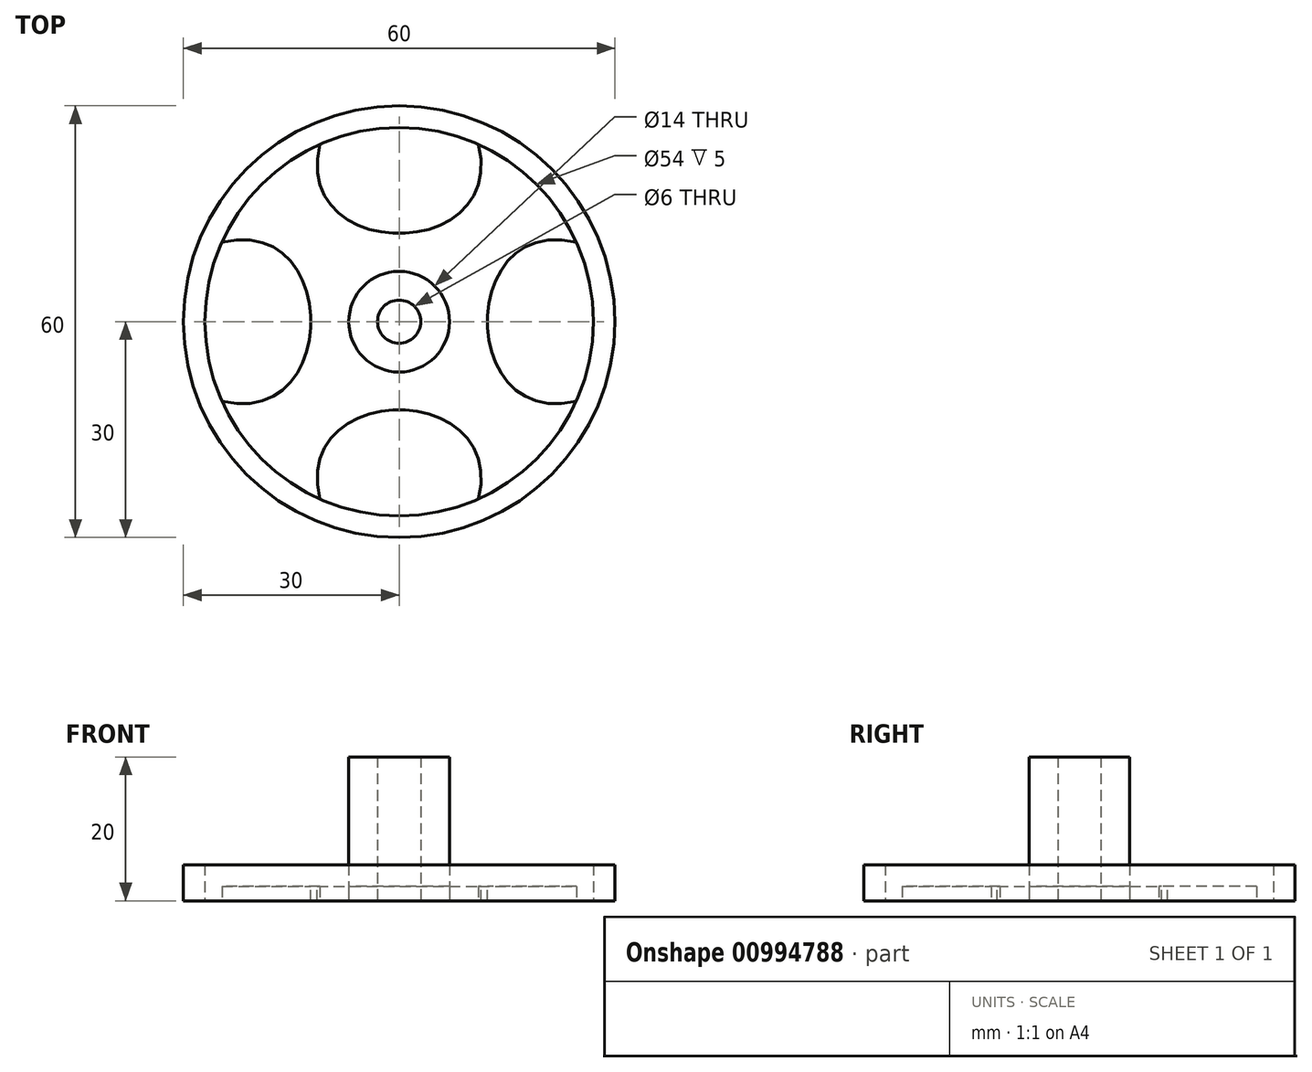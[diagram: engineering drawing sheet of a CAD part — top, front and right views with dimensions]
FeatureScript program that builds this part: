
annotation { "Feature Type Name" : "Feature", "Feature Type Description" : "" }
export const myFeature = defineFeature(function(context is Context, id is Id, definition is map)
    precondition{}
    {
        {
            var Q0;
            Q0=qCreatedBy(makeId("Top.planeOp"),FACE);
            var sketch = newSketch(context, id + "F0", { "sketchPlane" : qUnion([Q0])});
            skCircle(sketch, "E0", {"center": v(0, 0) * mm, "radius": 30 * mm});
            skCircle(sketch, "E1", {"center": v(0, 0) * mm, "radius": 27 * mm});
            skCircle(sketch, "E2", {"center": v(0, 0) * mm, "radius": 7 * mm});
            skCircle(sketch, "E3", {"center": v(0, 0) * mm, "radius": 3 * mm});
            skLineSegment(sketch, "E4", {"start": v(-43.77, 43.77) * mm, "end": v(46.4, -46.4) * mm, "construction": true});
            skLineSegment(sketch, "E5", {"start": v(40.6, 40.6) * mm, "end": v(-43.15, -43.15) * mm, "construction": true});
            skFitSpline(sketch, "E6", {"points": [v(-11.04, 24.64) * mm, v(11.04, 24.64) * mm], "startDerivative": vector(-11.88, -49.5) * mm, "endDerivative": vector(-11.88, 49.5) * mm});
            skFitSpline(sketch, "E7.MirrorCS", {"points": [v(-11.04, -24.64) * mm, v(11.04, -24.64) * mm], "startDerivative": vector(-11.88, 49.5) * mm, "endDerivative": vector(-11.88, -49.5) * mm});
            skFitSpline(sketch, "E8.MirrorCS", {"points": [v(-24.64, -11.04) * mm, v(-24.64, 11.04) * mm], "startDerivative": vector(49.5, -11.88) * mm, "endDerivative": vector(-49.5, -11.88) * mm});
            skFitSpline(sketch, "E9.MirrorCS", {"points": [v(24.64, 11.04) * mm, v(24.64, -11.04) * mm], "startDerivative": vector(-49.5, 11.88) * mm, "endDerivative": vector(49.5, 11.88) * mm});
            skSolve(sketch);
        }
        {
            var Q0;
            Q0=makeQuery(id+"F0.imprint","IMPRINT",FACE,{"disambiguationData":[TD([[makeQuery(id+"F0.imprint","IMPRINT",EDGE,{"derivedFrom":sQuery(id+"F0.wireOp",EDGE,"E0")}),1.0]])]});
            var Q1;
            Q1=makeQuery(id+"F0.imprint","IMPRINT",FACE,{"disambiguationData":[TD([[makeQuery(id+"F0.imprint","IMPRINT",EDGE,{"derivedFrom":sQuery(id+"F0.wireOp",EDGE,"E3")}),-1.0]])]});
            var Q2;
            {var subQ0=sQuery(id+"F0.wireOp",EDGE,"c8918afa-5bd7-44cf-8a52-512a02345781");Q2=makeQuery(id+"F0.imprint","IMPRINT",FACE,{"disambiguationData":[TD([[makeQuery(id+"F0.imprint","IMPRINT",EDGE,{"derivedFrom":subQ0}),-1.0]])]});}
            extrude(context, id + "F1", {"entities" : qUnion([Q0, Q1, Q2]), "depth" : 5 * mm, "offsetDistance" : 25 * mm});
        }
        {
            var Q0;
            Q0=makeQuery(id+"F0.imprint","IMPRINT",FACE,{"disambiguationData":[TD([[makeQuery(id+"F0.imprint","IMPRINT",EDGE,{"derivedFrom":sQuery(id+"F0.wireOp",EDGE,"E2")}),-1.0]])]});
            extrude(context, id + "F2", {"entities" : qUnion([Q0]), "depth" : 2 * mm, "offsetDistance" : 25 * mm});
        }
        {
            var Q0;
            Q0=makeQuery(id+"F1.opExtrude","CAP_FACE",FACE,{"disambiguationData":[OSD([sQuery(id+"F0.wireOp",EDGE,"E2"),sQuery(id+"F0.wireOp",EDGE,"E3")])],"isStart":false});
            extrude(context, id + "F3", {"entities" : qUnion([Q0]), "operationType" : NewBodyOperationType.ADD, "depth" : 15 * mm, "offsetDistance" : 25 * mm});
        }
    });
